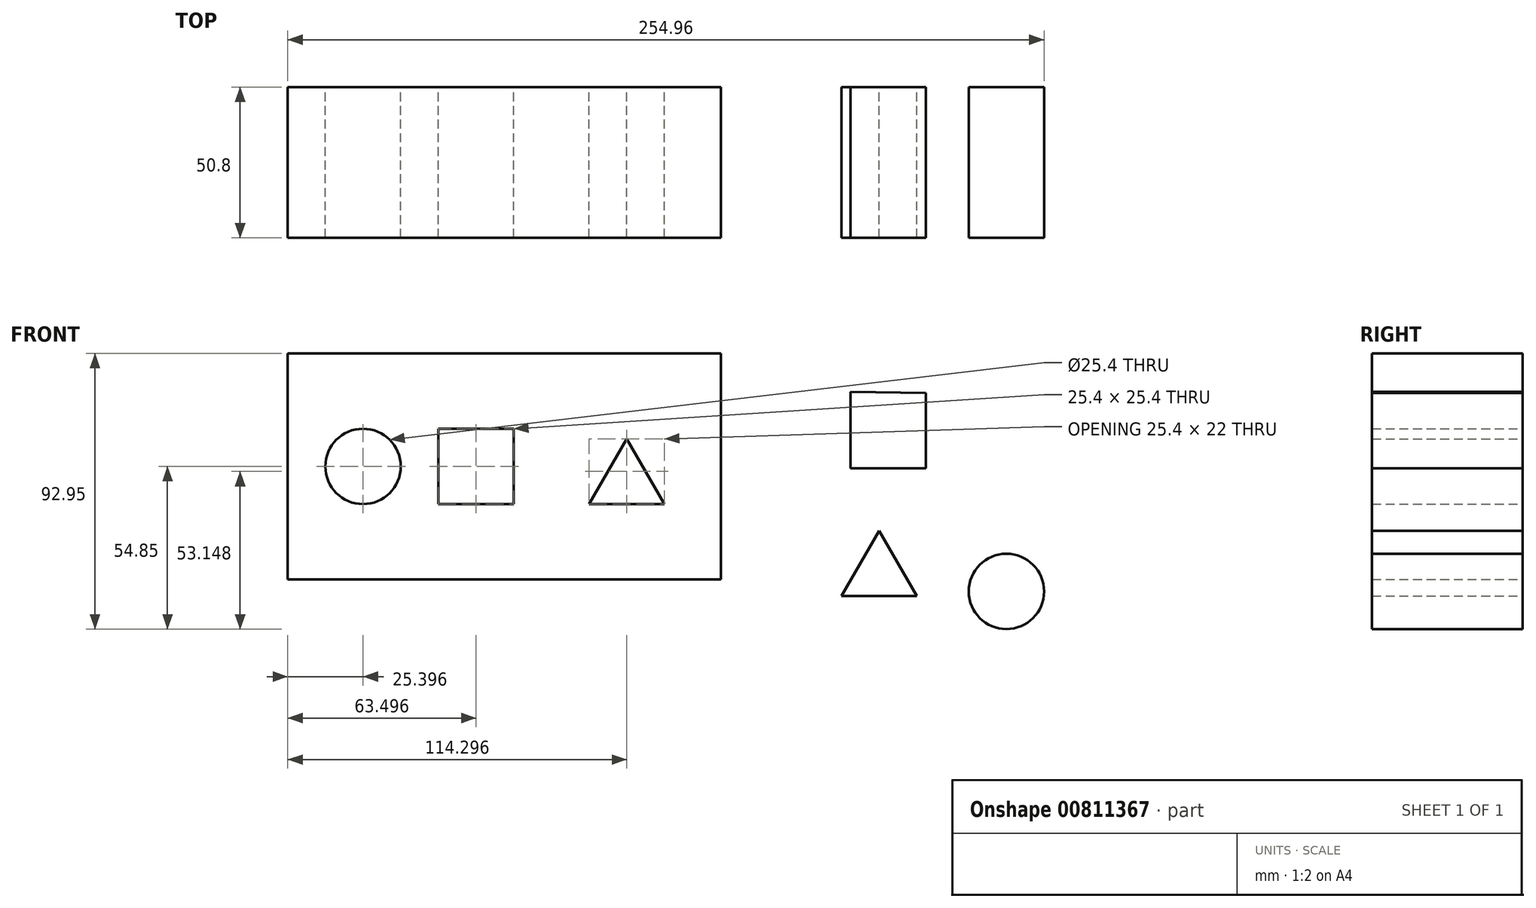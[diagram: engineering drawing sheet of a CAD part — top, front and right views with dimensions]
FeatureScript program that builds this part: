
annotation { "Feature Type Name" : "Feature", "Feature Type Description" : "" }
export const myFeature = defineFeature(function(context is Context, id is Id, definition is map)
    precondition{}
    {
        {
            var Q0;
            Q0=qCreatedBy(makeId("Front.planeOp"),FACE);
            var sketch = newSketch(context, id + "F0", { "sketchPlane" : qUnion([Q0])});
            skLineSegment(sketch, "E0", {"start": v(-156.3, 50.8) * mm, "end": v(-156.3, -25.4) * mm});
            skLineSegment(sketch, "E1", {"start": v(-156.3, -25.4) * mm, "end": v(-10.24, -25.4) * mm});
            skLineSegment(sketch, "E2", {"start": v(-10.24, -25.4) * mm, "end": v(-10.24, 50.8) * mm});
            skLineSegment(sketch, "E3", {"start": v(-10.24, 50.8) * mm, "end": v(-156.3, 50.8) * mm});
            skCircle(sketch, "E4", {"center": v(-130.9, 12.7) * mm, "radius": 12.7 * mm});
            skLineSegment(sketch, "E5", {"start": v(-80.1, 25.4) * mm, "end": v(-80.1, 0) * mm});
            skLineSegment(sketch, "E6", {"start": v(-105.5, 0) * mm, "end": v(-80.1, 0) * mm});
            skLineSegment(sketch, "E7", {"start": v(-105.5, 0) * mm, "end": v(-105.5, 25.4) * mm});
            skLineSegment(sketch, "E8", {"start": v(-80.1, 25.4) * mm, "end": v(-105.5, 25.4) * mm});
            skLineSegment(sketch, "E9", {"start": v(-42, 22) * mm, "end": v(-54.7, 0) * mm});
            skLineSegment(sketch, "E10", {"start": v(-54.7, 0) * mm, "end": v(-29.3, 0) * mm});
            skLineSegment(sketch, "E11", {"start": v(-29.3, 0) * mm, "end": v(-42, 22) * mm});
            skLineSegment(sketch, "E12", {"start": v(33.4, 37.86) * mm, "end": v(33.4, 12.02) * mm});
            skLineSegment(sketch, "E13", {"start": v(33.4, 12.02) * mm, "end": v(58.8, 12.02) * mm});
            skLineSegment(sketch, "E14", {"start": v(58.8, 12.02) * mm, "end": v(58.8, 37.42) * mm});
            skLineSegment(sketch, "E15", {"start": v(58.8, 37.42) * mm, "end": v(33.4, 37.86) * mm});
            skLineSegment(sketch, "E16", {"start": v(43.03, -9) * mm, "end": v(30.33, -31) * mm});
            skLineSegment(sketch, "E17", {"start": v(30.33, -31) * mm, "end": v(55.73, -31) * mm});
            skLineSegment(sketch, "E18", {"start": v(55.73, -31) * mm, "end": v(43.03, -9) * mm});
            skCircle(sketch, "E19", {"center": v(85.97, -29.45) * mm, "radius": 12.7 * mm});
            skSolve(sketch);
        }
        {
            var Q0;
            Q0=makeQuery(id+"F0.imprint","IMPRINT",FACE,{"disambiguationData":[TD([[makeQuery(id+"F0.imprint","IMPRINT",EDGE,{"derivedFrom":sQuery(id+"F0.wireOp",EDGE,"E0")}),1.0]])]});
            var Q1;
            Q1=makeQuery(id+"F0.imprint","IMPRINT",FACE,{"disambiguationData":[TD([[makeQuery(id+"F0.imprint","IMPRINT",EDGE,{"derivedFrom":sQuery(id+"F0.wireOp",EDGE,"E12")}),1.0]])]});
            var Q2;
            Q2=makeQuery(id+"F0.imprint","IMPRINT",FACE,{"disambiguationData":[TD([[makeQuery(id+"F0.imprint","IMPRINT",EDGE,{"derivedFrom":sQuery(id+"F0.wireOp",EDGE,"E16")}),1.0]])]});
            var Q3;
            Q3=makeQuery(id+"F0.imprint","IMPRINT",FACE,{"disambiguationData":[TD([[makeQuery(id+"F0.imprint","IMPRINT",EDGE,{"derivedFrom":sQuery(id+"F0.wireOp",EDGE,"E19")}),1.0]])]});
            extrude(context, id + "F1", {"entities" : qUnion([Q0, Q1, Q2, Q3]), "depth" : 50.8 * mm, "offsetDistance" : 25.4 * mm});
        }
    });
